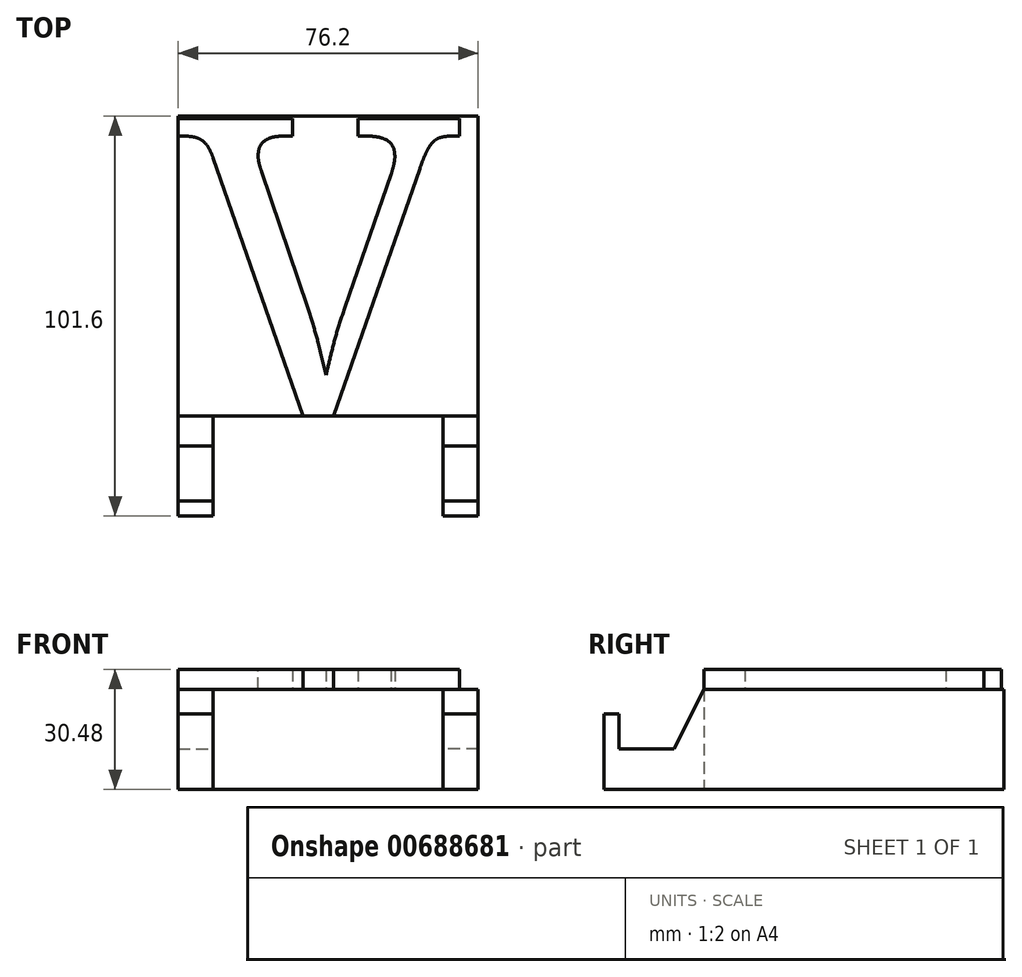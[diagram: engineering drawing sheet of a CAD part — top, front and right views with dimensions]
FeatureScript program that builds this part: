
annotation { "Feature Type Name" : "Feature", "Feature Type Description" : "" }
export const myFeature = defineFeature(function(context is Context, id is Id, definition is map)
    precondition{}
    {
        {
            var Q0;
            Q0=qCreatedBy(makeId("Front.planeOp"),FACE);
            var sketch = newSketch(context, id + "F0", { "sketchPlane" : qUnion([Q0])});
            skLineSegment(sketch, "E0", {"start": v(0, 0) * mm, "end": v(76.2, 0) * mm});
            skLineSegment(sketch, "E1", {"start": v(76.2, 0) * mm, "end": v(76.2, 25.4) * mm});
            skLineSegment(sketch, "E2", {"start": v(76.2, 25.4) * mm, "end": v(0, 25.4) * mm});
            skLineSegment(sketch, "E3", {"start": v(0, 25.4) * mm, "end": v(0, 0) * mm});
            skSolve(sketch);
        }
        {
            var Q0;
            Q0 = qSketchRegion(id + "F0", true);
            extrude(context, id + "F1", {"entities" : qUnion([Q0]), "depth" : 76.2 * mm, "offsetDistance" : 25.4 * mm});
        }
        {
            var Q0;
            Q0=makeQuery(id+"F1.opExtrude","CAP_FACE",FACE,{"disambiguationData":[OSD([sQuery(id+"F0.wireOp",EDGE,"E0"),sQuery(id+"F0.wireOp",EDGE,"E1"),sQuery(id+"F0.wireOp",EDGE,"E2"),sQuery(id+"F0.wireOp",EDGE,"E3")])],"isStart":false});
            var sketch = newSketch(context, id + "F2", { "sketchPlane" : qUnion([Q0])});
            skLineSegment(sketch, "E4", {"start": v(0, 25.4) * mm, "end": v(8.9, 25.4) * mm});
            skLineSegment(sketch, "E5", {"start": v(8.9, 25.4) * mm, "end": v(8.9, 0) * mm});
            skLineSegment(sketch, "E6", {"start": v(8.9, 0) * mm, "end": v(0, 0) * mm});
            skLineSegment(sketch, "E7", {"start": v(0, 0) * mm, "end": v(0, 25.4) * mm});
            skSolve(sketch);
        }
        {
            var Q0;
            Q0 = qSketchRegion(id + "F2", true);
            extrude(context, id + "F3", {"entities" : qUnion([Q0]), "operationType" : NewBodyOperationType.ADD, "depth" : 25.4 * mm, "offsetDistance" : 25.4 * mm});
        }
        {
            var Q0;
            Q0=makeQuery(id+"F3.opExtrude","SWEPT_FACE",FACE,{"disambiguationData":[OSD([sQuery(id+"F2.wireOp",EDGE,"E5")])]});
            var sketch = newSketch(context, id + "F4", { "sketchPlane" : qUnion([Q0])});
            skLineSegment(sketch, "E8", {"start": v(-101.6, 19.14) * mm, "end": v(-93.98, 19.14) * mm});
            skLineSegment(sketch, "E9", {"start": v(-93.98, 19.14) * mm, "end": v(-93.98, 10.25) * mm});
            skLineSegment(sketch, "E10", {"start": v(-93.98, 10.25) * mm, "end": v(-83.82, 10.25) * mm});
            skLineSegment(sketch, "E11", {"start": v(-83.82, 10.25) * mm, "end": v(-76.2, 25.4) * mm});
            skLineSegment(sketch, "E12", {"start": v(-76.2, 25.4) * mm, "end": v(-101.6, 25.4) * mm});
            skLineSegment(sketch, "E13", {"start": v(-101.6, 25.4) * mm, "end": v(-101.6, 19.14) * mm});
            skSolve(sketch);
        }
        {
            var Q0;
            Q0 = qSketchRegion(id + "F4", true);
            extrude(context, id + "F5", {"entities" : qUnion([Q0]), "operationType" : NewBodyOperationType.REMOVE, "oppositeDirection" : true, "depth" : 25.4 * mm, "offsetDistance" : 25.4 * mm});
        }
        {
            var Q0;
            Q0=makeQuery(id+"F3.opExtrude","SWEPT_FACE",FACE,{"disambiguationData":[OSD([sQuery(id+"F2.wireOp",EDGE,"E5")])]});
            var sketch = newSketch(context, id + "F6", { "sketchPlane" : qUnion([Q0])});
            skLineSegment(sketch, "E14", {"start": v(-97.8, 19.14) * mm, "end": v(-97.8, 10.25) * mm});
            skLineSegment(sketch, "E15", {"start": v(-97.8, 10.25) * mm, "end": v(-93.98, 10.25) * mm});
            skLineSegment(sketch, "E16", {"start": v(-93.98, 10.25) * mm, "end": v(-93.98, 19.14) * mm});
            skLineSegment(sketch, "E17", {"start": v(-93.98, 19.14) * mm, "end": v(-97.8, 19.14) * mm});
            skSolve(sketch);
        }
        {
            var Q0;
            Q0 = qSketchRegion(id + "F6", true);
            extrude(context, id + "F7", {"entities" : qUnion([Q0]), "operationType" : NewBodyOperationType.REMOVE, "oppositeDirection" : true, "depth" : 25.4 * mm, "offsetDistance" : 25.4 * mm});
        }
        {
            var Q0;
            Q0=makeQuery(id+"F1.opExtrude","CAP_FACE",FACE,{"disambiguationData":[OSD([sQuery(id+"F0.wireOp",EDGE,"E0"),sQuery(id+"F0.wireOp",EDGE,"E1"),sQuery(id+"F0.wireOp",EDGE,"E2"),sQuery(id+"F0.wireOp",EDGE,"E3")])],"isStart":false});
            var sketch = newSketch(context, id + "F8", { "sketchPlane" : qUnion([Q0])});
            skLineSegment(sketch, "E18", {"start": v(76.2, 25.4) * mm, "end": v(67.31, 25.4) * mm});
            skLineSegment(sketch, "E19", {"start": v(67.31, 25.4) * mm, "end": v(67.31, 0) * mm});
            skLineSegment(sketch, "E20", {"start": v(67.31, 0) * mm, "end": v(76.2, 0) * mm});
            skLineSegment(sketch, "E21", {"start": v(76.2, 0) * mm, "end": v(76.2, 25.4) * mm});
            skSolve(sketch);
        }
        {
            var Q0;
            Q0 = qSketchRegion(id + "F8", true);
            extrude(context, id + "F9", {"entities" : qUnion([Q0]), "operationType" : NewBodyOperationType.ADD, "depth" : 25.4 * mm, "offsetDistance" : 25.4 * mm});
        }
        {
            var Q0;
            Q0=makeQuery(id+"F9.opExtrude","SWEPT_FACE",FACE,{"disambiguationData":[OSD([sQuery(id+"F8.wireOp",EDGE,"E19")])]});
            var sketch = newSketch(context, id + "F10", { "sketchPlane" : qUnion([Q0])});
            skLineSegment(sketch, "E22", {"start": v(76.2, 25.4) * mm, "end": v(83.8, 10.3) * mm});
            skLineSegment(sketch, "E23", {"start": v(83.8, 10.3) * mm, "end": v(97.8, 10.3) * mm});
            skLineSegment(sketch, "E24", {"start": v(97.8, 10.3) * mm, "end": v(97.8, 19.2) * mm});
            skLineSegment(sketch, "E25", {"start": v(97.8, 19.2) * mm, "end": v(101.6, 19.2) * mm});
            skLineSegment(sketch, "E26", {"start": v(101.6, 19.2) * mm, "end": v(101.6, 25.4) * mm});
            skLineSegment(sketch, "E27", {"start": v(101.6, 25.4) * mm, "end": v(76.2, 25.4) * mm});
            skSolve(sketch);
        }
        {
            var Q0;
            Q0 = qSketchRegion(id + "F10", true);
            extrude(context, id + "F11", {"entities" : qUnion([Q0]), "operationType" : NewBodyOperationType.REMOVE, "oppositeDirection" : true, "depth" : 25.4 * mm, "offsetDistance" : 25.4 * mm});
        }
        {
            var Q0;
            Q0=makeQuery(id+"F9.boolean.opBoolean","MERGE",FACE,{"derivedFrom":[makeQuery(id+"F3.boolean.opBoolean","MERGE",FACE,{"derivedFrom":[makeQuery(id+"F1.opExtrude","SWEPT_FACE",FACE,{"disambiguationData":[OSD([sQuery(id+"F0.wireOp",EDGE,"E2")])]}),makeQuery(id+"F3.opExtrude","SWEPT_FACE",FACE,{"disambiguationData":[OSD([sQuery(id+"F2.wireOp",EDGE,"E4")])]})]}),makeQuery(id+"F9.opExtrude","SWEPT_FACE",FACE,{"disambiguationData":[OSD([sQuery(id+"F8.wireOp",EDGE,"E18")])]})]});
            var sketch = newSketch(context, id + "F12", { "sketchPlane" : qUnion([Q0])});
            skText(sketch, "E28", { "text": "V", "fontName": "NotoSerif-Regular.ttf"});
            const initialGuessF12  = {"E28": [0, -0.0762, 1, 0, 0.0762]};
            skSetInitialGuess(sketch, initialGuessF12);
            skSolve(sketch);
        }
        {
            var Q0;
            Q0 = qSketchRegion(id + "F12", true);
            extrude(context, id + "F13", {"entities" : qUnion([Q0]), "depth" : 5.08 * mm, "offsetDistance" : 25.4 * mm});
        }
    });
